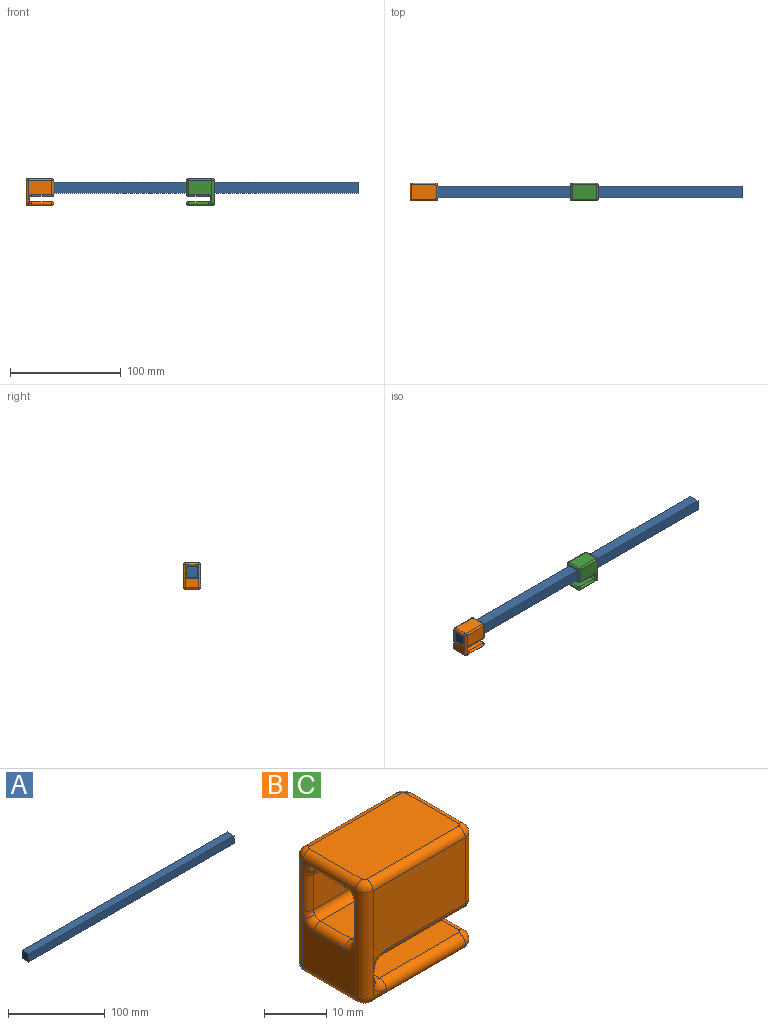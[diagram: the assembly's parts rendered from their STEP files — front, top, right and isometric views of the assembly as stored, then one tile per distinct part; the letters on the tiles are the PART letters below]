
ASSEMBLY  parts=3 mates=2
PART A: 6 faces, bbox 300x10x10 mm
  f0: plane 300x10mm, normal (0,0,-1), area 3000mm2, adj f1,f3,f4,f5
  f1: plane 300x10mm, normal (0,1,0), area 3000mm2, adj f0,f2,f4,f5
  f2: plane 300x10mm, normal (0,0,1), area 3000mm2, adj f1,f3,f4,f5
  f3: plane 300x10mm, normal (0,-1,0), area 3000mm2, adj f0,f2,f4,f5
  f4: plane 10x10mm, normal (1,0,0), area 100mm2, adj f0,f1,f2,f3
  f5: plane 10x10mm, normal (-1,0,0), area 100mm2, adj f0,f1,f2,f3
PART B: 82 faces, bbox 25.3x16.1x24 mm
  f0: plane 2.5x1.34mm, normal (1,0,0), area 1mm2, adj f25,f44,f78
  f1: plane 2.5x1.34mm, normal (1,0,0), area 1mm2, adj f25,f52,f77
  f2: plane 2.5x1.34mm, normal (1,0,0), area 1mm2, adj f24,f44,f76
  f3: plane 12x9.34mm, normal (-1,0,0), area 98mm2, adj f22,f23,f30,f69,f70,f71
  f4: plane 2.5x1.34mm, normal (-1,0,0), area 1mm2, adj f23,f53,f61
  f5: plane 21x14.7mm, normal (0,-1,0), area 274.5mm2, adj f22,f24,f38,f40,f49
  f6: plane 21x14.7mm, normal (0,1,0), area 274.5mm2, adj f23,f25,f47,f48,f56
  f7: plane 18.5x13mm, normal (0,0,-1), area 240.4mm2, adj f20,f40,f42,f44,f46,f48
  f8: plane 3x1.7mm, normal (0,1,0), area 1.5mm2, adj f23,f36,f39
  f9: plane 22x13mm, normal (0,0,1), area 285.8mm2, adj f49,f50,f51,f52,f53,f54,f55,f56
  f10: plane 3x1.7mm, normal (0,-1,0), area 1.5mm2, adj f22,f26,f29
  f11: plane 22x7mm, normal (0,0,-1), area 154mm2, adj f52,f53,f57,f60
  f12: plane 22.17x7mm, normal (0,-1,0), area 155.2mm2, adj f57,f58,f65,f81
  f13: plane 22x7mm, normal (0,0,1), area 154mm2, adj f44,f58,f59,f71
  f14: plane 22.17x7mm, normal (0,1,0), area 155.2mm2, adj f59,f60,f66,f72
  f15: plane 2.5x1.34mm, normal (1,0,0), area 1mm2, adj f24,f52,f75
  f16: plane 2.5x1.34mm, normal (-1,0,0), area 1mm2, adj f22,f53,f62
  f17: plane 13.17x1mm, normal (1,0,0), area 13.2mm2, adj f20,f21,f35,f43
  f18: plane 22x13mm, normal (0,0,-1), area 285.8mm2, adj f26,f27,f28,f30,f31,f33,f34,f36
  f19: plane 18.5x13mm, normal (0,0,1), area 240.4mm2, adj f21,f26,f28,f31,f34,f36
  f20: cylinder r=2mm len=13.17mm, axis (0,-1,0), area 40.9mm2, adj f7,f17,f37,f38,f45,f47
  f21: cylinder r=2mm len=13.17mm, axis (0,1,0), area 40.9mm2, adj f17,f19,f29,f32,f39,f41
  f22: cylinder r=2mm len=21mm, axis (0,0,-1), area 66mm2, adj f3,f5,f10,f16,f27,f32,f35,f37
  f23: cylinder r=2mm len=21mm, axis (0,0,1), area 66mm2, adj f3,f4,f6,f8,f33,f41,f43,f45
  f24: cylinder r=2mm len=13mm, axis (0,0,1), area 40.8mm2, adj f2,f5,f15,f42,f50,f72,f73,f74
  f25: cylinder r=2mm len=13mm, axis (0,0,-1), area 40.8mm2, adj f0,f1,f6,f46,f54,f79,f80,f81
  f26: cylinder r=1.5mm len=21mm, axis (1,0,0), area 91.9mm2, adj f10,f18,f19,f27,f28,f29
  f27: torus R=0.5mm, axis (0,0,-1), area 5.4mm2, adj f18,f22,f26,f30
  f28: torus R=0.5mm, axis (0,0,-1), area 10.8mm2, adj f18,f19,f26,f31
  f29: torus R=3.5mm, axis (0,-1,0), area 6.2mm2, adj f10,f21,f26,f32
  f30: cylinder r=1.5mm len=12mm, axis (0,1,0), area 28.3mm2, adj f3,f18,f27,f33
  f31: cylinder r=1.5mm len=12mm, axis (0,1,0), area 56.5mm2, adj f18,f19,f28,f34
  f32: bspline ~2.19x1.57mm, area 2.6mm2, adj f21,f22,f29,f35
  f33: torus R=0.5mm, axis (0,0,-1), area 5.4mm2, adj f18,f23,f30,f36
  f34: torus R=0.5mm, axis (0,0,-1), area 10.8mm2, adj f18,f19,f31,f36
  f35: cylinder r=1.5mm len=1.41mm, axis (0,0,1), area 1.8mm2, adj f17,f22,f32,f37
  f36: cylinder r=1.5mm len=21mm, axis (-1,0,0), area 91.9mm2, adj f8,f18,f19,f33,f34,f39
  f37: bspline ~2.19x1.57mm, area 2.6mm2, adj f20,f22,f35,f38
  f38: torus R=3.5mm, axis (0,-1,0), area 6.2mm2, adj f5,f20,f37,f40
  f39: torus R=3.5mm, axis (0,-1,0), area 6.2mm2, adj f8,f21,f36,f41
  f40: cylinder r=1.5mm len=18mm, axis (-1,0,0), area 42.4mm2, adj f5,f7,f38,f42
  f41: bspline ~2.19x1.57mm, area 2.6mm2, adj f21,f23,f39,f43
  f42: torus R=0.5mm, axis (0,0,-1), area 5.4mm2, adj f7,f24,f40,f44
  f43: cylinder r=1.5mm len=1.41mm, axis (0,0,1), area 1.8mm2, adj f17,f23,f41,f45
  f44: cylinder r=1.5mm len=12mm, axis (0,-1,0), area 44.8mm2, adj f0,f2,f7,f13,f42,f46,f76,f78
  f45: bspline ~2.19x1.57mm, area 2.6mm2, adj f20,f23,f43,f47
  f46: torus R=0.5mm, axis (0,0,-1), area 5.4mm2, adj f7,f25,f44,f48
  f47: torus R=3.5mm, axis (0,-1,0), area 6.2mm2, adj f6,f20,f45,f48
  f48: cylinder r=1.5mm len=18mm, axis (1,0,0), area 42.4mm2, adj f6,f7,f46,f47
  f49: cylinder r=1.5mm len=21mm, axis (1,0,0), area 49.5mm2, adj f5,f9,f50,f51
  f50: torus R=0.5mm, axis (0,0,-1), area 5.4mm2, adj f9,f24,f49,f52
  f51: torus R=0.5mm, axis (0,0,-1), area 5.4mm2, adj f9,f22,f49,f53
  f52: cylinder r=1.5mm len=12mm, axis (0,1,0), area 44.8mm2, adj f1,f9,f11,f15,f50,f54,f75,f77
  f53: cylinder r=1.5mm len=12mm, axis (0,-1,0), area 44.8mm2, adj f4,f9,f11,f16,f51,f55,f61,f62
  f54: torus R=0.5mm, axis (0,0,-1), area 5.4mm2, adj f9,f25,f52,f56
  f55: torus R=0.5mm, axis (0,0,-1), area 5.4mm2, adj f9,f23,f53,f56
  f56: cylinder r=1.5mm len=21mm, axis (-1,0,0), area 49.5mm2, adj f6,f9,f54,f55
  f57: cylinder r=1.5mm len=22.17mm, axis (1,0,0), area 51.9mm2, adj f11,f12,f61,f63,f77,f79
  f58: cylinder r=1.5mm len=22.17mm, axis (-1,0,0), area 51.9mm2, adj f12,f13,f67,f69,f78,f80
  f59: cylinder r=1.5mm len=22.17mm, axis (1,0,0), area 51.9mm2, adj f13,f14,f68,f70,f74,f76
  f60: cylinder r=1.5mm len=22.17mm, axis (-1,0,0), area 51.9mm2, adj f11,f14,f62,f64,f73,f75
  f61: torus R=3mm, axis (1,0,0), area 4.7mm2, adj f4,f53,f57,f63
  f62: torus R=3mm, axis (1,0,0), area 4.7mm2, adj f16,f53,f60,f64
  f63: bspline ~2.3x1.66mm, area 2.3mm2, adj f23,f57,f61,f65
  f64: bspline ~2.3x1.66mm, area 2.3mm2, adj f22,f60,f62,f66
  f65: cylinder r=1.5mm len=7mm, axis (0,0,1), area 12.9mm2, adj f12,f23,f63,f67
  f66: cylinder r=1.5mm len=7mm, axis (0,0,1), area 12.9mm2, adj f14,f22,f64,f68
  f67: bspline ~2.3x1.66mm, area 2.3mm2, adj f23,f58,f65,f69
  f68: bspline ~2.3x1.66mm, area 2.3mm2, adj f22,f59,f66,f70
  f69: torus R=3mm, axis (1,0,0), area 4.7mm2, adj f3,f58,f67,f71
  f70: torus R=3mm, axis (1,0,0), area 4.7mm2, adj f3,f59,f68,f71
  f71: cylinder r=1.5mm len=7mm, axis (0,-1,0), area 16.5mm2, adj f3,f13,f69,f70
  f72: cylinder r=1.5mm len=7mm, axis (0,0,1), area 12.9mm2, adj f14,f24,f73,f74
  f73: bspline ~2.3x1.66mm, area 2.3mm2, adj f24,f60,f72,f75
  f74: bspline ~2.3x1.66mm, area 2.3mm2, adj f24,f59,f72,f76
  f75: torus R=3mm, axis (1,0,0), area 4.7mm2, adj f15,f52,f60,f73
  f76: torus R=3mm, axis (1,0,0), area 4.7mm2, adj f2,f44,f59,f74
  f77: torus R=3mm, axis (1,0,0), area 4.7mm2, adj f1,f52,f57,f79
  f78: torus R=3mm, axis (1,0,0), area 4.7mm2, adj f0,f44,f58,f80
  f79: bspline ~2.3x1.66mm, area 2.3mm2, adj f25,f57,f77,f81
  f80: bspline ~2.3x1.66mm, area 2.3mm2, adj f25,f58,f78,f81
  f81: cylinder r=1.5mm len=7mm, axis (0,0,1), area 12.9mm2, adj f12,f25,f79,f80
PART C: same geometry as B
PLACE A at identity
PLACE B t=(0,0,0.01)mm
PLACE C rot(axis=(0,0,1),180deg) t=(170,0,0.01)mm
MATE slider C.f3 <-> A.f5  axis (1,0,0) through (170,0,-10.4)mm
MATE slider A.f5 <-> B.f3  axis (-1,0,0) through (0,0,0)mm
